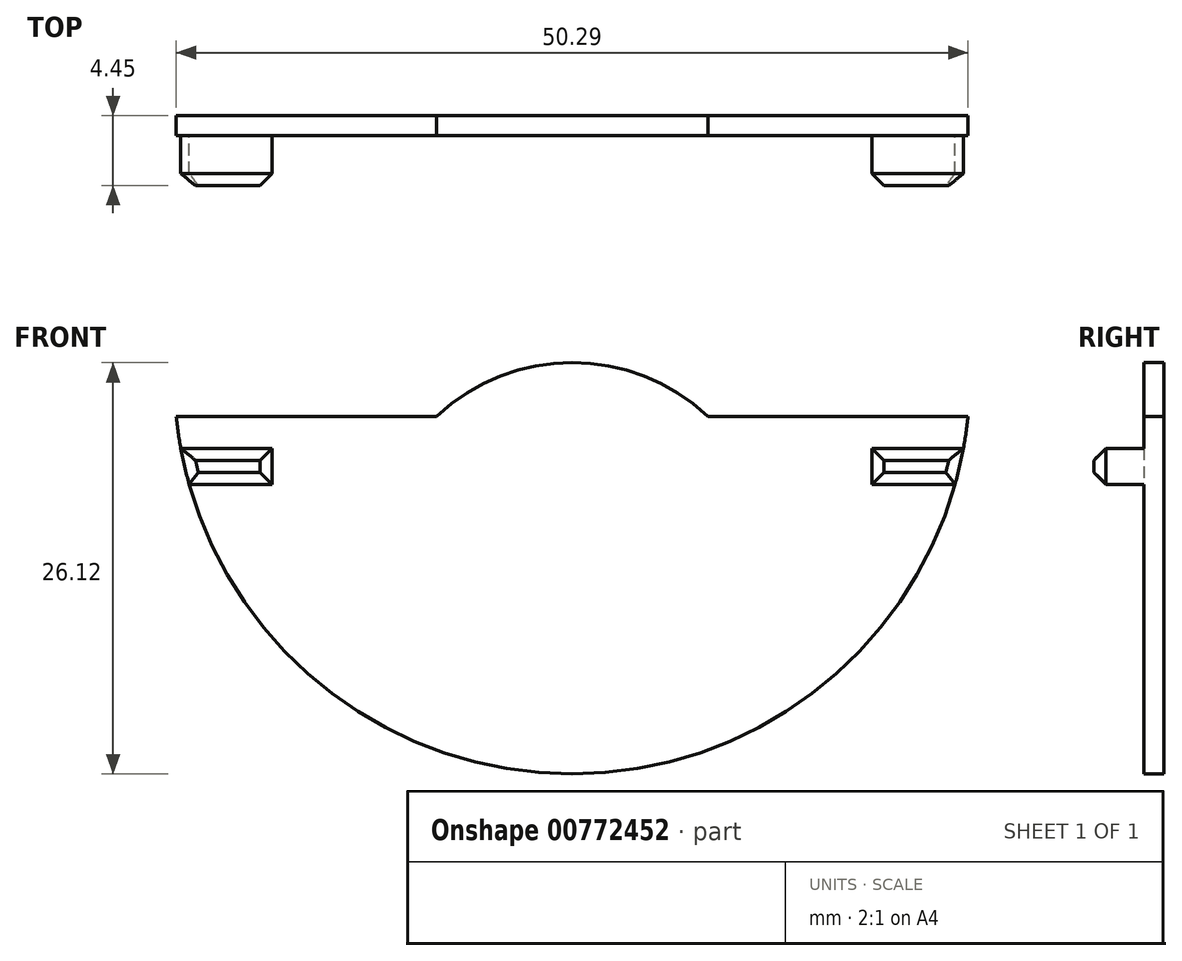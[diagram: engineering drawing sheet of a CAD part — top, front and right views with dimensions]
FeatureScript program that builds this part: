
annotation { "Feature Type Name" : "Feature", "Feature Type Description" : "" }
export const myFeature = defineFeature(function(context is Context, id is Id, definition is map)
    precondition{}
    {
        {
            var Q0;
            Q0=qCreatedBy(makeId("Front.planeOp"),FACE);
            var sketch = newSketch(context, id + "F0", { "sketchPlane" : qUnion([Q0])});
            skArc(sketch, "E0", {"start": v(-25.27, 0) * mm, "mid": v(0, -25.77) * mm, "end": v(25.27, 0) * mm});
            skLineSegment(sketch, "E1.bottom", {"start": v(-19.05, -5.09) * mm, "end": v(-26.67, -5.09) * mm});
            skLineSegment(sketch, "E1.top", {"start": v(-19.05, -7.37) * mm, "end": v(-26.67, -7.37) * mm});
            skLineSegment(sketch, "E1.left", {"start": v(-19.05, -5.09) * mm, "end": v(-19.05, -7.37) * mm});
            skLineSegment(sketch, "E1.right", {"start": v(-26.67, -5.09) * mm, "end": v(-26.67, -7.37) * mm});
            skPoint(sketch, "E1.middle", {"position": v(-22.86, -6.23) * mm});
            skLineSegment(sketch, "E2.bottom", {"start": v(26.67, -5.09) * mm, "end": v(19.05, -5.09) * mm});
            skLineSegment(sketch, "E2.top", {"start": v(26.67, -7.37) * mm, "end": v(19.05, -7.37) * mm});
            skLineSegment(sketch, "E2.left", {"start": v(26.67, -5.09) * mm, "end": v(26.67, -7.37) * mm});
            skLineSegment(sketch, "E2.right", {"start": v(19.05, -5.09) * mm, "end": v(19.05, -7.37) * mm});
            skPoint(sketch, "E2.middle", {"position": v(22.86, -6.23) * mm});
            skCircle(sketch, "E3", {"center": v(0, -12.24) * mm, "radius": 12.6 * mm});
            skLineSegment(sketch, "E4", {"start": v(-25.15, -3.05) * mm, "end": v(25.14, -3.05) * mm});
            skSolve(sketch);
        }
        {
            var Q0;
            {var subQ1=sQuery(id+"F0.wireOp",EDGE,"E0");Q0=makeQuery(id+"F0.imprint","IMPRINT",FACE,{"disambiguationData":[TD([[makeQuery(id+"F0.imprint","IMPRINT",EDGE,{"derivedFrom":subQ1}),1.0]])]});}
            var Q1;
            {var subQ0=sQuery(id+"F0.wireOp",EDGE,"aVV66S4D-bi7w-QqUD-R8Yy-OoWORB9SKqqg");var subQ1=sQuery(id+"F0.wireOp",EDGE,"JYtZChIu-rhpb-k2LN-Vukp-1MHqIPhgMpcL");var subQ2=makeQuery(id+"F0.imprint","INTERSECT",VERTEX,{"disambiguationData":[OD(0.0)],"derivedFrom":[subQ1,subQ0]});Q1=makeQuery(id+"F0.imprint","IMPRINT",FACE,{"disambiguationData":[TD([[makeQuery(id+"F0.imprint","IMPRINT",EDGE,{"disambiguationData":[TD([[subQ2,-1.0]])],"derivedFrom":subQ1}),-1.0]])]});}
            var Q2;
            {var subQ0=sQuery(id+"F0.wireOp",EDGE,"aVV66S4D-bi7w-QqUD-R8Yy-OoWORB9SKqqg");var subQ1=sQuery(id+"F0.wireOp",EDGE,"JYtZChIu-rhpb-k2LN-Vukp-1MHqIPhgMpcL");var subQ2=makeQuery(id+"F0.imprint","INTERSECT",VERTEX,{"disambiguationData":[OD(0.0)],"derivedFrom":[subQ1,subQ0]});Q2=makeQuery(id+"F0.imprint","IMPRINT",FACE,{"disambiguationData":[TD([[makeQuery(id+"F0.imprint","IMPRINT",EDGE,{"disambiguationData":[TD([[subQ2,-1.0]])],"derivedFrom":subQ1}),1.0]])]});}
            var Q3;
            {var subQ0=sQuery(id+"F0.wireOp",EDGE,"E3");var subQ1=sQuery(id+"F0.wireOp",EDGE,"SfgjYYAp-p2Ls-tOR0-qbJ5-YI2unhik5UT1");var subQ2=makeQuery(id+"F0.imprint","INTERSECT",VERTEX,{"disambiguationData":[OD(0.0)],"derivedFrom":[subQ1,subQ0]});Q3=makeQuery(id+"F0.imprint","IMPRINT",FACE,{"disambiguationData":[TD([[makeQuery(id+"F0.imprint","IMPRINT",EDGE,{"disambiguationData":[TD([[subQ2,-1.0]])],"derivedFrom":subQ1}),-1.0]])]});}
            var Q4;
            {var subQ0=sQuery(id+"F0.wireOp",EDGE,"E3");var subQ1=sQuery(id+"F0.wireOp",EDGE,"SfgjYYAp-p2Ls-tOR0-qbJ5-YI2unhik5UT1");var subQ2=makeQuery(id+"F0.imprint","INTERSECT",VERTEX,{"disambiguationData":[OD(0.0)],"derivedFrom":[subQ1,subQ0]});Q4=makeQuery(id+"F0.imprint","IMPRINT",FACE,{"disambiguationData":[TD([[makeQuery(id+"F0.imprint","IMPRINT",EDGE,{"disambiguationData":[TD([[subQ2,-1.0]])],"derivedFrom":subQ1}),1.0]])]});}
            var Q5;
            {var subQ0=sQuery(id+"F0.wireOp",EDGE,"E4");var subQ1=sQuery(id+"F0.wireOp",EDGE,"E3");var subQ2=makeQuery(id+"F0.imprint","INTERSECT",VERTEX,{"disambiguationData":[OD(0.0)],"derivedFrom":[subQ1,subQ0]});Q5=makeQuery(id+"F0.imprint","IMPRINT",FACE,{"disambiguationData":[TD([[makeQuery(id+"F0.imprint","IMPRINT",EDGE,{"disambiguationData":[TD([[subQ2,1.0]])],"derivedFrom":subQ1}),1.0]])]});}
            var Q6;
            {var subQ0=sQuery(id+"F0.wireOp",EDGE,"E4");var subQ1=sQuery(id+"F0.wireOp",EDGE,"E3");var subQ2=makeQuery(id+"F0.imprint","INTERSECT",VERTEX,{"disambiguationData":[OD(0.0)],"derivedFrom":[subQ1,subQ0]});Q6=makeQuery(id+"F0.imprint","IMPRINT",FACE,{"disambiguationData":[TD([[makeQuery(id+"F0.imprint","IMPRINT",EDGE,{"disambiguationData":[TD([[subQ2,-1.0]])],"derivedFrom":subQ1}),1.0]])]});}
            extrude(context, id + "F1", {"entities" : qUnion([Q0, Q1, Q2, Q3, Q4, Q5, Q6]), "depth" : 1.27 * mm, "offsetDistance" : 25.4 * mm});
        }
        {
            var Q0;
            {var subQ5=sQuery(id+"F0.wireOp",EDGE,"E1.left");Q0=makeQuery(id+"F0.imprint","IMPRINT",FACE,{"disambiguationData":[TD([[makeQuery(id+"F0.imprint","IMPRINT",EDGE,{"derivedFrom":subQ5}),-1.0]])]});}
            var Q1;
            {var subQ5=sQuery(id+"F0.wireOp",EDGE,"E2.right");Q1=makeQuery(id+"F0.imprint","IMPRINT",FACE,{"disambiguationData":[TD([[makeQuery(id+"F0.imprint","IMPRINT",EDGE,{"derivedFrom":subQ5}),1.0]])]});}
            extrude(context, id + "F2", {"entities" : qUnion([Q0, Q1]), "operationType" : NewBodyOperationType.ADD, "depth" : 4.44 * mm, "offsetDistance" : 25.4 * mm});
        }
        {
            var Q0;
            Q0=makeQuery(id+"F2.opExtrude","CAP_EDGE",EDGE,{"disambiguationData":[OSD([sQuery(id+"F0.wireOp",EDGE,"E2.bottom")])],"isStart":false});
            var Q1;
            Q1=makeQuery(id+"F2.opExtrude","CAP_EDGE",EDGE,{"disambiguationData":[OSD([sQuery(id+"F0.wireOp",EDGE,"E2.right")])],"isStart":false});
            var Q2;
            Q2=makeQuery(id+"F2.opExtrude","CAP_EDGE",EDGE,{"disambiguationData":[OSD([sQuery(id+"F0.wireOp",EDGE,"E2.top")])],"isStart":false});
            var Q3;
            {var subQ0=sQuery(id+"F0.wireOp",EDGE,"E0");Q3=makeQuery(id+"F2.opExtrude","CAP_EDGE",EDGE,{"disambiguationData":[OSD([subQ0]),TDD([makeQuery(id+"F0.imprint","IMPRINT",EDGE,{"disambiguationData":[TD([[makeQuery(id+"F0.imprint","INTERSECT",VERTEX,{"derivedFrom":[subQ0,sQuery(id+"F0.wireOp",EDGE,"E2.top")]}),-1.0]])],"derivedFrom":subQ0})])],"isStart":false});}
            var Q4;
            Q4=makeQuery(id+"F2.opExtrude","CAP_EDGE",EDGE,{"disambiguationData":[OSD([sQuery(id+"F0.wireOp",EDGE,"E1.top")])],"isStart":false});
            var Q5;
            {var subQ0=sQuery(id+"F0.wireOp",EDGE,"E0");Q5=makeQuery(id+"F2.opExtrude","CAP_EDGE",EDGE,{"disambiguationData":[OSD([subQ0]),TDD([makeQuery(id+"F0.imprint","IMPRINT",EDGE,{"disambiguationData":[TD([[makeQuery(id+"F0.imprint","INTERSECT",VERTEX,{"derivedFrom":[subQ0,sQuery(id+"F0.wireOp",EDGE,"E1.bottom")]}),-1.0]])],"derivedFrom":subQ0})])],"isStart":false});}
            var Q6;
            Q6=makeQuery(id+"F2.opExtrude","CAP_EDGE",EDGE,{"disambiguationData":[OSD([sQuery(id+"F0.wireOp",EDGE,"E1.left")])],"isStart":false});
            var Q7;
            Q7=makeQuery(id+"F2.opExtrude","CAP_EDGE",EDGE,{"disambiguationData":[OSD([sQuery(id+"F0.wireOp",EDGE,"E1.bottom")])],"isStart":false});
            chamfer(context, id + "F3", {"entities" : qUnion([Q0, Q1, Q2, Q3, Q4, Q5, Q6, Q7]), "chamferType" : ChamferType.OFFSET_ANGLE, "width" : 0.76 * mm, "oppositeDirection" : false, "angle" : 45 * degree, "tangentPropagation" : true});
        }
    });
